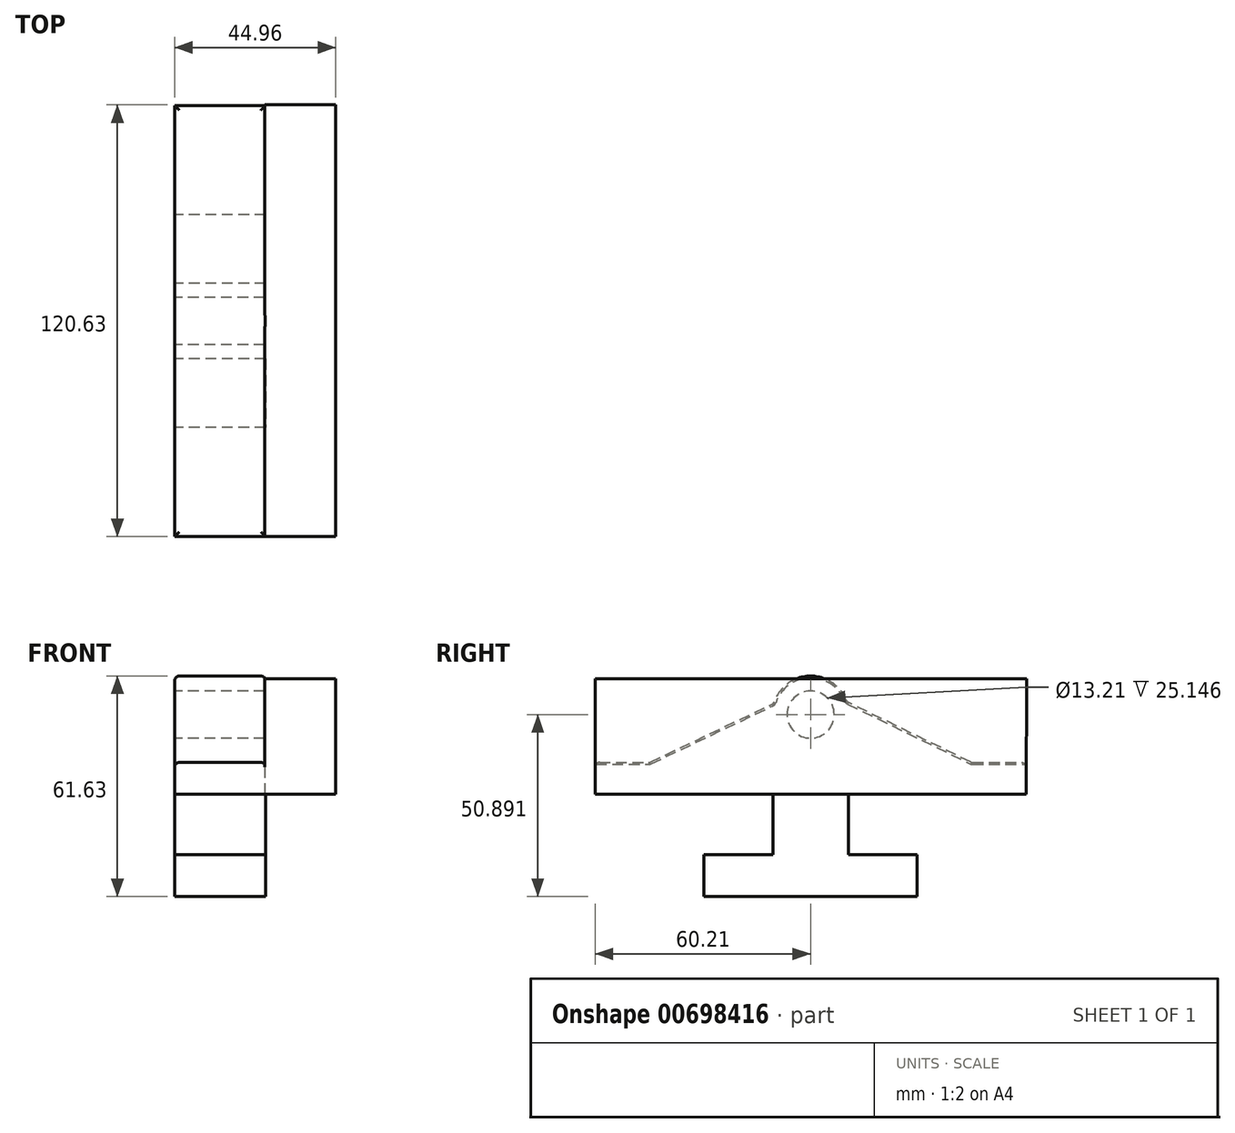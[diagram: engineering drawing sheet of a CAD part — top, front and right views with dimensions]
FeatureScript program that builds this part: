
annotation { "Feature Type Name" : "Feature", "Feature Type Description" : "" }
export const myFeature = defineFeature(function(context is Context, id is Id, definition is map)
    precondition{}
    {
        {
            var Q0;
            Q0=qCreatedBy(makeId("Right.planeOp"),FACE);
            var sketch = newSketch(context, id + "F0", { "sketchPlane" : qUnion([Q0])});
            skLineSegment(sketch, "E0.bottom", {"start": v(-60.21, 19.51) * mm, "end": v(-44.97, 19.51) * mm});
            skLineSegment(sketch, "E0.right", {"start": v(60.21, 19.51) * mm, "end": v(60.21, 10.7) * mm});
            skLineSegment(sketch, "E1", {"start": v(0, 10.94) * mm, "end": v(0, -17.98) * mm, "construction": true});
            skPoint(sketch, "E2.MirrorP", {"position": v(0, -6.87) * mm});
            skCircle(sketch, "E3", {"center": v(0, 32.91) * mm, "radius": 10.74 * mm});
            skCircle(sketch, "E4", {"center": v(0, 32.91) * mm, "radius": 6.6 * mm});
            skLineSegment(sketch, "E5", {"start": v(44.97, 19.51) * mm, "end": v(10.13, 36.5) * mm});
            skLineSegment(sketch, "E6", {"start": v(-44.97, 19.51) * mm, "end": v(-10.3, 35.98) * mm});
            skLineSegment(sketch, "E7.trimOffspring", {"start": v(44.97, 19.51) * mm, "end": v(60.21, 19.51) * mm});
            skLineSegment(sketch, "E8", {"start": v(-60.21, 19.51) * mm, "end": v(-60.21, 10.7) * mm});
            skLineSegment(sketch, "E9", {"start": v(-60.21, 10.7) * mm, "end": v(-10.54, 10.7) * mm});
            skLineSegment(sketch, "E10", {"start": v(-10.54, 10.7) * mm, "end": v(-10.54, -6.19) * mm});
            skLineSegment(sketch, "E11", {"start": v(-10.54, -6.19) * mm, "end": v(-29.75, -6.19) * mm});
            skLineSegment(sketch, "E12", {"start": v(-29.75, -6.19) * mm, "end": v(-29.75, -17.98) * mm});
            skLineSegment(sketch, "E13", {"start": v(-29.75, -17.98) * mm, "end": v(0, -17.98) * mm});
            skLineSegment(sketch, "E14.MirrorCS", {"start": v(10.54, -6.19) * mm, "end": v(29.75, -6.19) * mm});
            skLineSegment(sketch, "E15.MirrorCS", {"start": v(29.75, -6.19) * mm, "end": v(29.75, -17.98) * mm});
            skLineSegment(sketch, "E16.MirrorCS", {"start": v(10.54, 10.7) * mm, "end": v(10.54, -6.19) * mm});
            skLineSegment(sketch, "E17.MirrorCS", {"start": v(60.21, 10.7) * mm, "end": v(10.54, 10.7) * mm});
            skLineSegment(sketch, "E18.MirrorCS", {"start": v(29.75, -17.98) * mm, "end": v(0, -17.98) * mm});
            skSolve(sketch);
        }
        {
            var Q0;
            Q0 = qSketchRegion(id + "F0", true);
            extrude(context, id + "F1", {"entities" : qUnion([Q0]), "depth" : 25.4 * mm, "offsetDistance" : 25.4 * mm});
        }
        {
            var Q0;
            Q0=makeQuery(id+"F1.opExtrude","CAP_EDGE",EDGE,{"disambiguationData":[OSD([sQuery(id+"F0.wireOp",EDGE,"E6")])],"isStart":false});
            var Q1;
            Q1=makeQuery(id+"F1.opExtrude","CAP_EDGE",EDGE,{"disambiguationData":[OSD([sQuery(id+"F0.wireOp",EDGE,"E3")])],"isStart":false});
            var Q2;
            Q2=makeQuery(id+"F1.opExtrude","CAP_EDGE",EDGE,{"disambiguationData":[OSD([sQuery(id+"F0.wireOp",EDGE,"E5")])],"isStart":false});
            var Q3;
            Q3=makeQuery(id+"F1.opExtrude","CAP_EDGE",EDGE,{"disambiguationData":[OSD([sQuery(id+"F0.wireOp",EDGE,"E7.trimOffspring")])],"isStart":false});
            var Q4;
            Q4=makeQuery(id+"F1.opExtrude","CAP_EDGE",EDGE,{"disambiguationData":[OSD([sQuery(id+"F0.wireOp",EDGE,"E0.bottom")])],"isStart":false});
            var Q5;
            Q5=makeQuery(id+"F1.opExtrude","SWEPT_EDGE",EDGE,{"disambiguationData":[OSD([sQuery(id+"F0.wireOp",EDGE,"E0.bottom"),sQuery(id+"F0.wireOp",EDGE,"E6")])]});
            var Q6;
            Q6=makeQuery(id+"F1.opExtrude","SWEPT_EDGE",EDGE,{"disambiguationData":[OSD([sQuery(id+"F0.wireOp",EDGE,"E0.bottom"),sQuery(id+"F0.wireOp",EDGE,"E8")])]});
            var Q7;
            Q7=makeQuery(id+"F1.opExtrude","CAP_EDGE",EDGE,{"disambiguationData":[OSD([sQuery(id+"F0.wireOp",EDGE,"E0.bottom")])],"isStart":true});
            var Q8;
            Q8=makeQuery(id+"F1.opExtrude","CAP_EDGE",EDGE,{"disambiguationData":[OSD([sQuery(id+"F0.wireOp",EDGE,"E6")])],"isStart":true});
            var Q9;
            Q9=makeQuery(id+"F1.opExtrude","CAP_EDGE",EDGE,{"disambiguationData":[OSD([sQuery(id+"F0.wireOp",EDGE,"E3")])],"isStart":true});
            var Q10;
            Q10=makeQuery(id+"F1.opExtrude","CAP_EDGE",EDGE,{"disambiguationData":[OSD([sQuery(id+"F0.wireOp",EDGE,"E5")])],"isStart":true});
            var Q11;
            Q11=makeQuery(id+"F1.opExtrude","CAP_EDGE",EDGE,{"disambiguationData":[OSD([sQuery(id+"F0.wireOp",EDGE,"E7.trimOffspring")])],"isStart":true});
            var Q12;
            Q12=makeQuery(id+"F1.opExtrude","SWEPT_EDGE",EDGE,{"disambiguationData":[OSD([sQuery(id+"F0.wireOp",EDGE,"E0.right"),sQuery(id+"F0.wireOp",EDGE,"E7.trimOffspring")])]});
            var Q13;
            Q13=makeQuery(id+"F1.opExtrude","SWEPT_EDGE",EDGE,{"disambiguationData":[OSD([sQuery(id+"F0.wireOp",EDGE,"E5"),sQuery(id+"F0.wireOp",EDGE,"E7.trimOffspring")])]});
            var Q14;
            Q14=makeQuery(id+"F1.opExtrude","SWEPT_EDGE",EDGE,{"disambiguationData":[OSD([sQuery(id+"F0.wireOp",EDGE,"E3"),sQuery(id+"F0.wireOp",EDGE,"E6")])]});
            var Q15;
            Q15=makeQuery(id+"F1.opExtrude","SWEPT_EDGE",EDGE,{"disambiguationData":[OSD([sQuery(id+"F0.wireOp",EDGE,"E3"),sQuery(id+"F0.wireOp",EDGE,"E5")])]});
            fillet(context, id + "F2", {"entities" : qUnion([Q0, Q1, Q2, Q3, Q4, Q5, Q6, Q7, Q8, Q9, Q10, Q11, Q12, Q13, Q14, Q15]), "radius" : 1.27 * mm, "tangentPropagation" : true, "allowEdgeOverflow" : false});
        }
        {
            var Q0;
            Q0=makeQuery(id+"F1.opExtrude","CAP_FACE",FACE,{"disambiguationData":[OSD([sQuery(id+"F0.wireOp",EDGE,"E0.bottom"),sQuery(id+"F0.wireOp",EDGE,"E0.right"),sQuery(id+"F0.wireOp",EDGE,"E3"),sQuery(id+"F0.wireOp",EDGE,"E4"),sQuery(id+"F0.wireOp",EDGE,"E5"),sQuery(id+"F0.wireOp",EDGE,"E6"),sQuery(id+"F0.wireOp",EDGE,"E7.trimOffspring"),sQuery(id+"F0.wireOp",EDGE,"E8"),sQuery(id+"F0.wireOp",EDGE,"E9"),sQuery(id+"F0.wireOp",EDGE,"E10"),sQuery(id+"F0.wireOp",EDGE,"E11"),sQuery(id+"F0.wireOp",EDGE,"E12"),sQuery(id+"F0.wireOp",EDGE,"E13"),sQuery(id+"F0.wireOp",EDGE,"E14.MirrorCS"),sQuery(id+"F0.wireOp",EDGE,"E15.MirrorCS"),sQuery(id+"F0.wireOp",EDGE,"E16.MirrorCS"),sQuery(id+"F0.wireOp",EDGE,"E17.MirrorCS"),sQuery(id+"F0.wireOp",EDGE,"E18.MirrorCS")])],"isStart":false});
            cPlane(context, id + "F3", {"entities" : qUnion([Q0]), "cplaneType" : CPlaneType.OFFSET, "offset" : 19.56 * mm, "width" : 152.4 * mm, "height" : 152.4 * mm});
        }
        {
            var Q0;
            Q0=qCreatedBy(id+"F3.planeOp",FACE);
            var sketch = newSketch(context, id + "F4", { "sketchPlane" : qUnion([Q0])});
            skLineSegment(sketch, "E19.0.2", {"start": v(-60.21, 18.24) * mm, "end": v(-60.21, 10.7) * mm});
            skLineSegment(sketch, "E20", {"start": v(-60.21, 10.7) * mm, "end": v(-60.21, 42.9) * mm});
            skLineSegment(sketch, "E21", {"start": v(-60.21, 42.9) * mm, "end": v(60.42, 42.9) * mm});
            skLineSegment(sketch, "E22", {"start": v(-60.21, 10.7) * mm, "end": v(60.28, 10.7) * mm});
            skLineSegment(sketch, "E23", {"start": v(60.28, 10.7) * mm, "end": v(60.42, 42.9) * mm});
            skSolve(sketch);
        }
        {
            var Q0;
            {var subQ2=sQuery(id+"F4.wireOp",EDGE,"E21");Q0=makeQuery(id+"F4.imprint","IMPRINT",FACE,{"disambiguationData":[TD([[makeQuery(id+"F4.imprint","IMPRINT",EDGE,{"derivedFrom":subQ2}),-1.0]])]});}
            extrude(context, id + "F5", {"entities" : qUnion([Q0]), "operationType" : NewBodyOperationType.ADD, "oppositeDirection" : true, "depth" : 19.8 * mm, "offsetDistance" : 25.4 * mm});
        }
    });
